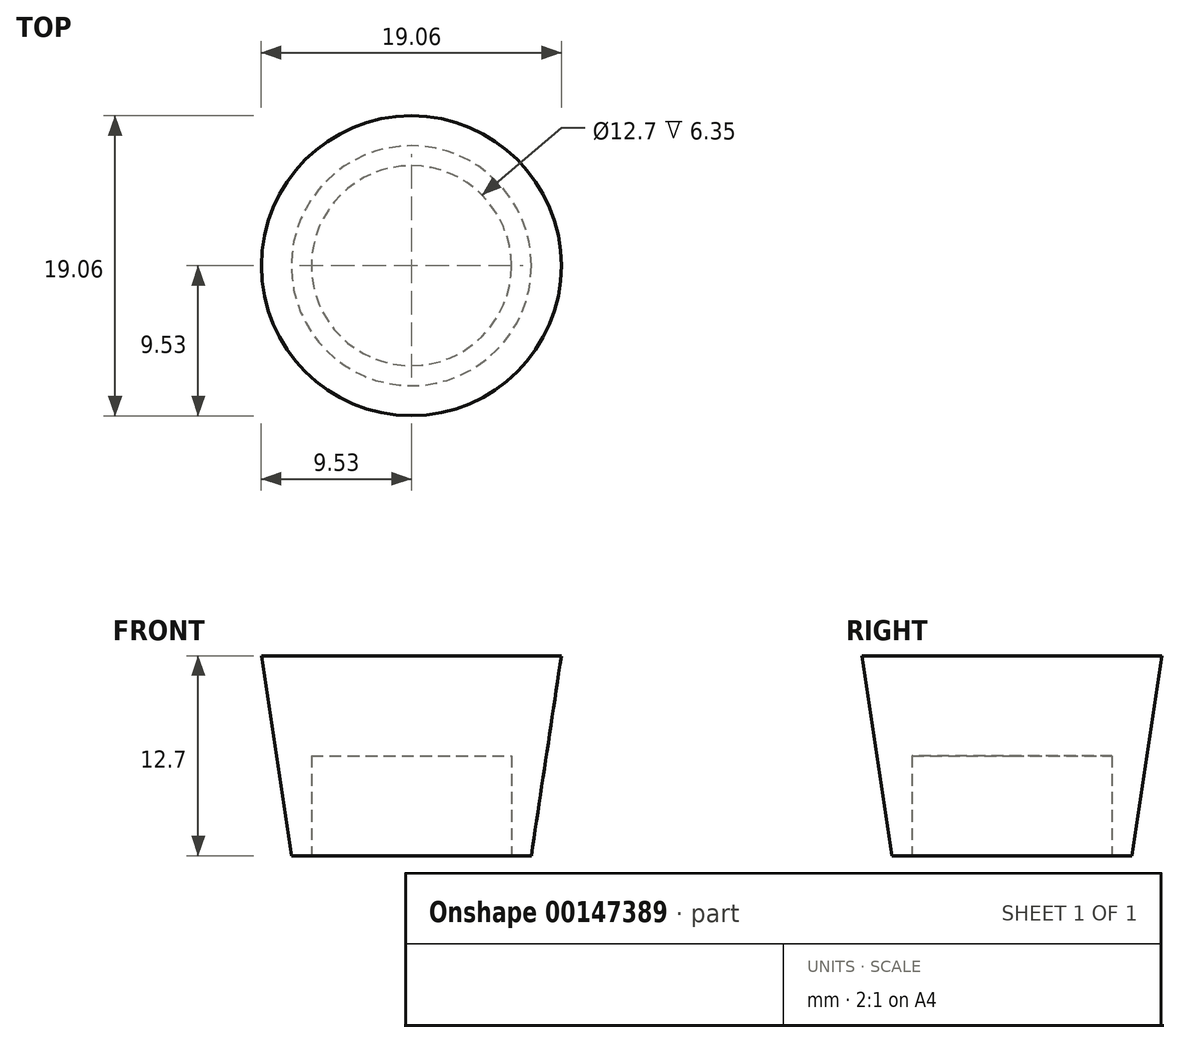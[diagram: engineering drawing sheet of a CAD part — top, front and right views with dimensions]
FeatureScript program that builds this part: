
annotation { "Feature Type Name" : "Feature", "Feature Type Description" : "" }
export const myFeature = defineFeature(function(context is Context, id is Id, definition is map)
    precondition{}
    {
        {
            var Q0;
            Q0=qCreatedBy(makeId("Top.planeOp"),FACE);
            var sketch = newSketch(context, id + "F0", { "sketchPlane" : qUnion([Q0])});
            skCircle(sketch, "E0", {"center": v(0, 0) * mm, "radius": 7.62 * mm});
            skSolve(sketch);
        }
        {
            var Q0;
            Q0=qCreatedBy(makeId("Top.planeOp"),FACE);
            cPlane(context, id + "F1", {"entities" : qUnion([Q0]), "cplaneType" : CPlaneType.OFFSET, "offset" : 12.7 * mm, "width" : 152.4 * mm, "height" : 152.4 * mm});
        }
        {
            var Q0;
            Q0=qCreatedBy(id+"F1.planeOp",FACE);
            var sketch = newSketch(context, id + "F2", { "sketchPlane" : qUnion([Q0])});
            skCircle(sketch, "E1", {"center": v(0, 0) * mm, "radius": 9.53 * mm});
            skSolve(sketch);
        }
        {
            var Q0;
            Q0 = qSketchRegion(id + "F0", true);
            var Q1;
            Q1 = qSketchRegion(id + "F2", true);
            loft(context, id + "F3", {"sheetProfilesArray" : [{ "sheetProfileEntities" : qUnion([Q0]) }, { "sheetProfileEntities" : qUnion([Q1]) }]});
        }
        {
            var Q0;
            Q0=makeQuery(id+"F3.opLoft","CAP_FACE",FACE,{"disambiguationData":[OSD([makeQuery(id+"F0.imprint","IMPRINT",FACE,{"disambiguationData":[TD([[makeQuery(id+"F0.imprint","IMPRINT",EDGE,{"derivedFrom":sQuery(id+"F0.wireOp",EDGE,"E0")}),1.0]])]})])],"isStart":true});
            var sketch = newSketch(context, id + "F4", { "sketchPlane" : qUnion([Q0])});
            skCircle(sketch, "E2", {"center": v(0, 0) * mm, "radius": 6.35 * mm});
            skSolve(sketch);
        }
        {
            var Q0;
            Q0 = qSketchRegion(id + "F4", true);
            extrude(context, id + "F5", {"entities" : qUnion([Q0]), "operationType" : NewBodyOperationType.REMOVE, "oppositeDirection" : true, "depth" : 6.35 * mm});
        }
    });
